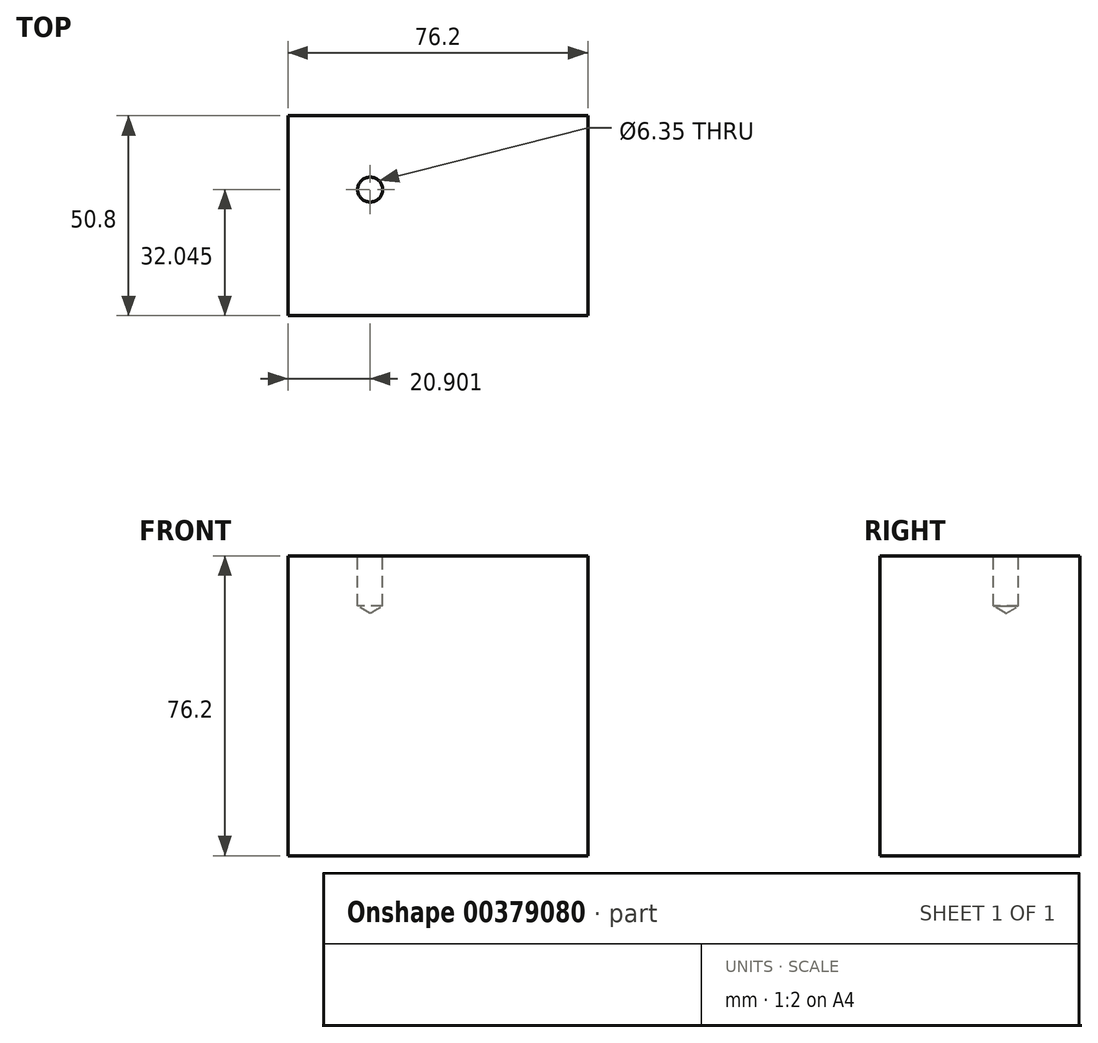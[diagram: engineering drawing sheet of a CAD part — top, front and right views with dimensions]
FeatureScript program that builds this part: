
annotation { "Feature Type Name" : "Feature", "Feature Type Description" : "" }
export const myFeature = defineFeature(function(context is Context, id is Id, definition is map)
    precondition{}
    {
        {
            var Q0;
            Q0=qCreatedBy(makeId("Top.planeOp"),FACE);
            var sketch = newSketch(context, id + "F0", { "sketchPlane" : qUnion([Q0])});
            skLineSegment(sketch, "E0.bottom", {"start": v(38.1, -25.4) * mm, "end": v(-38.1, -25.4) * mm});
            skLineSegment(sketch, "E0.top", {"start": v(38.1, 25.4) * mm, "end": v(-38.1, 25.4) * mm});
            skLineSegment(sketch, "E0.left", {"start": v(38.1, -25.4) * mm, "end": v(38.1, 25.4) * mm});
            skLineSegment(sketch, "E0.right", {"start": v(-38.1, -25.4) * mm, "end": v(-38.1, 25.4) * mm});
            skPoint(sketch, "E0.middle", {"position": v(0, 0) * mm});
            skSolve(sketch);
        }
        {
            var Q0;
            Q0=makeQuery(id+"F0.imprint","IMPRINT",FACE,{"disambiguationData":[TD([[makeQuery(id+"F0.imprint","IMPRINT",EDGE,{"derivedFrom":sQuery(id+"F0.wireOp",EDGE,"E0.bottom")}),-1.0]])]});
            extrude(context, id + "F1", {"entities" : qUnion([Q0]), "depth" : 76.2 * mm});
        }
        {
            var Q0;
            Q0=makeQuery(id+"F1.opExtrude","CAP_FACE",FACE,{"disambiguationData":[OSD([sQuery(id+"F0.wireOp",EDGE,"E0.bottom"),sQuery(id+"F0.wireOp",EDGE,"E0.top"),sQuery(id+"F0.wireOp",EDGE,"E0.left"),sQuery(id+"F0.wireOp",EDGE,"E0.right")])],"isStart":false});
            var sketch = newSketch(context, id + "F2", { "sketchPlane" : qUnion([Q0])});
            skPoint(sketch, "E1", {"position": v(-17.2, 6.65) * mm});
            skSolve(sketch);
        }
        {
            var Q0;
            Q0=sQuery(id+"F2.wireOp",VERTEX,"E1");
            var Q1;
            Q1=makeQuery(id+"F1.opExtrude","SWEPT_BODY",BODY,{"disambiguationData":[OSD([sQuery(id+"F0.wireOp",EDGE,"E0.bottom"),sQuery(id+"F0.wireOp",EDGE,"E0.top"),sQuery(id+"F0.wireOp",EDGE,"E0.left"),sQuery(id+"F0.wireOp",EDGE,"E0.right")])]});
            hole(context, id + "F3", {"style" : HoleStyle.SIMPLE, "endStyle" : HoleEndStyle.BLIND, "holeDiameter" : 6.35 * mm, "holeDepth" : 12.7 * mm, "isTappedThrough" : true, "tappedDepth" : 12.7 * mm, "tapClearance" : 3, "locations" : qUnion([Q0]), "scope" : qUnion([Q1])});
        }
    });
